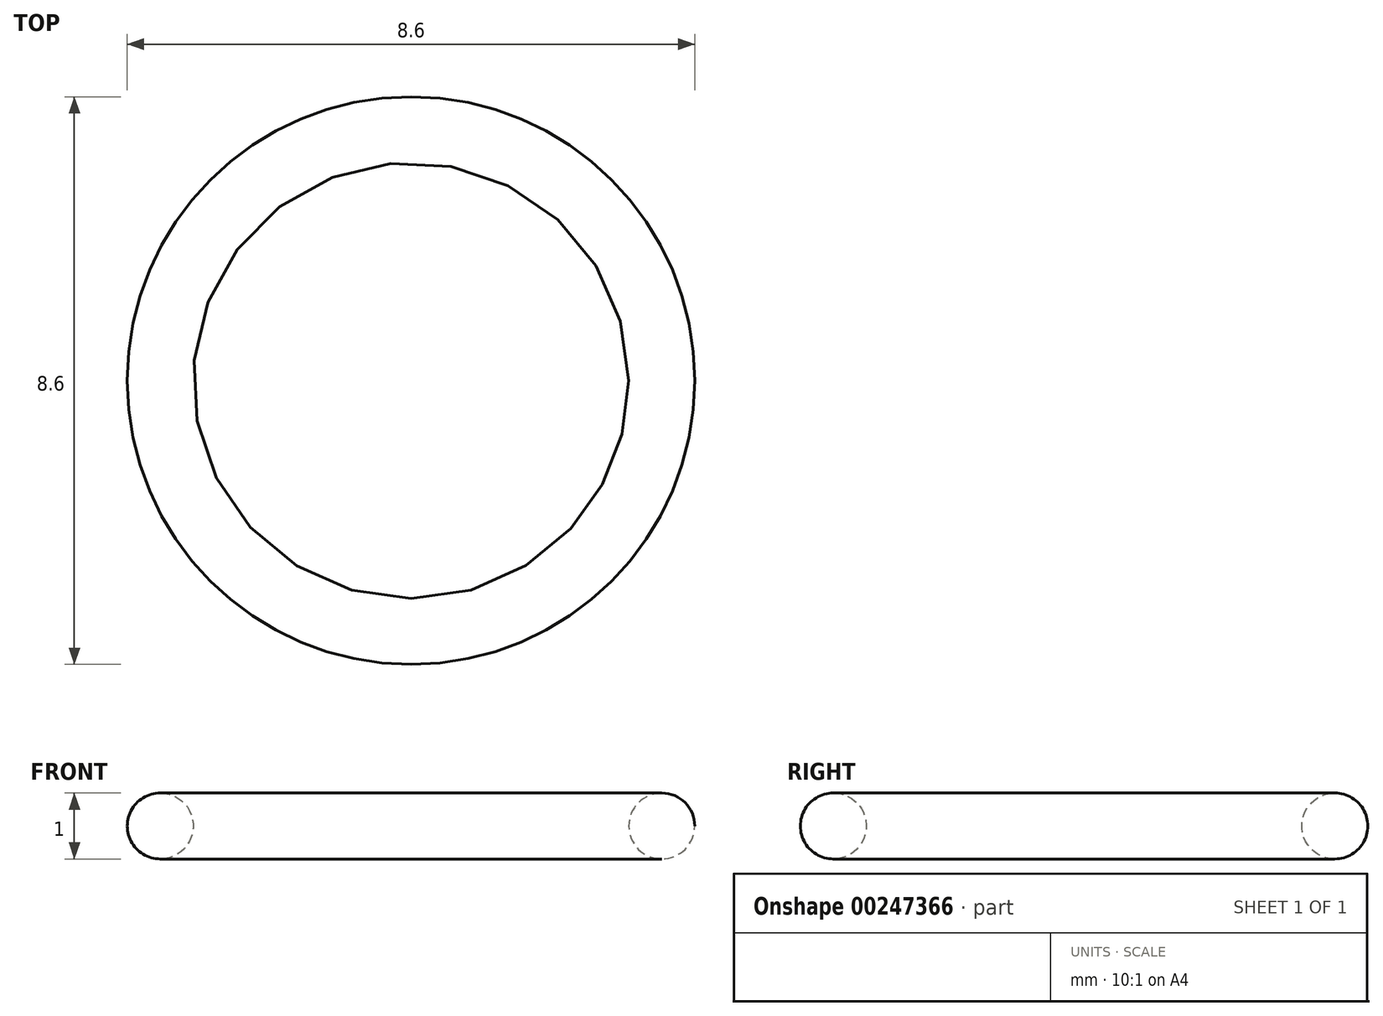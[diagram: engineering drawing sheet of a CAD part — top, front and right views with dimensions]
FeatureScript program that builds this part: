
annotation { "Feature Type Name" : "Feature", "Feature Type Description" : "" }
export const myFeature = defineFeature(function(context is Context, id is Id, definition is map)
    precondition{}
    {
        {
            var Q0;
            Q0=qCreatedBy(makeId("Front.planeOp"),FACE);
            var sketch = newSketch(context, id + "F0", { "sketchPlane" : qUnion([Q0])});
            skCircle(sketch, "E0", {"center": v(-3.8, 0) * mm, "radius": 0.5 * mm});
            skLineSegment(sketch, "E1", {"start": v(0, 1) * mm, "end": v(0, -1.87) * mm});
            skSolve(sketch);
        }
        {
            var Q0;
            Q0=makeQuery(id+"F0.imprint","IMPRINT",FACE,{"disambiguationData":[TD([[makeQuery(id+"F0.imprint","IMPRINT",EDGE,{"derivedFrom":sQuery(id+"F0.wireOp",EDGE,"E0")}),1.0]])]});
            var Q1;
            Q1=sQuery(id+"F0.wireOp",EDGE,"E1");
            revolve(context, id + "F1", {"entities" : qUnion([Q0]), "axis" : qUnion([Q1]), "revolveType" : RevolveType.FULL});
        }
    });
